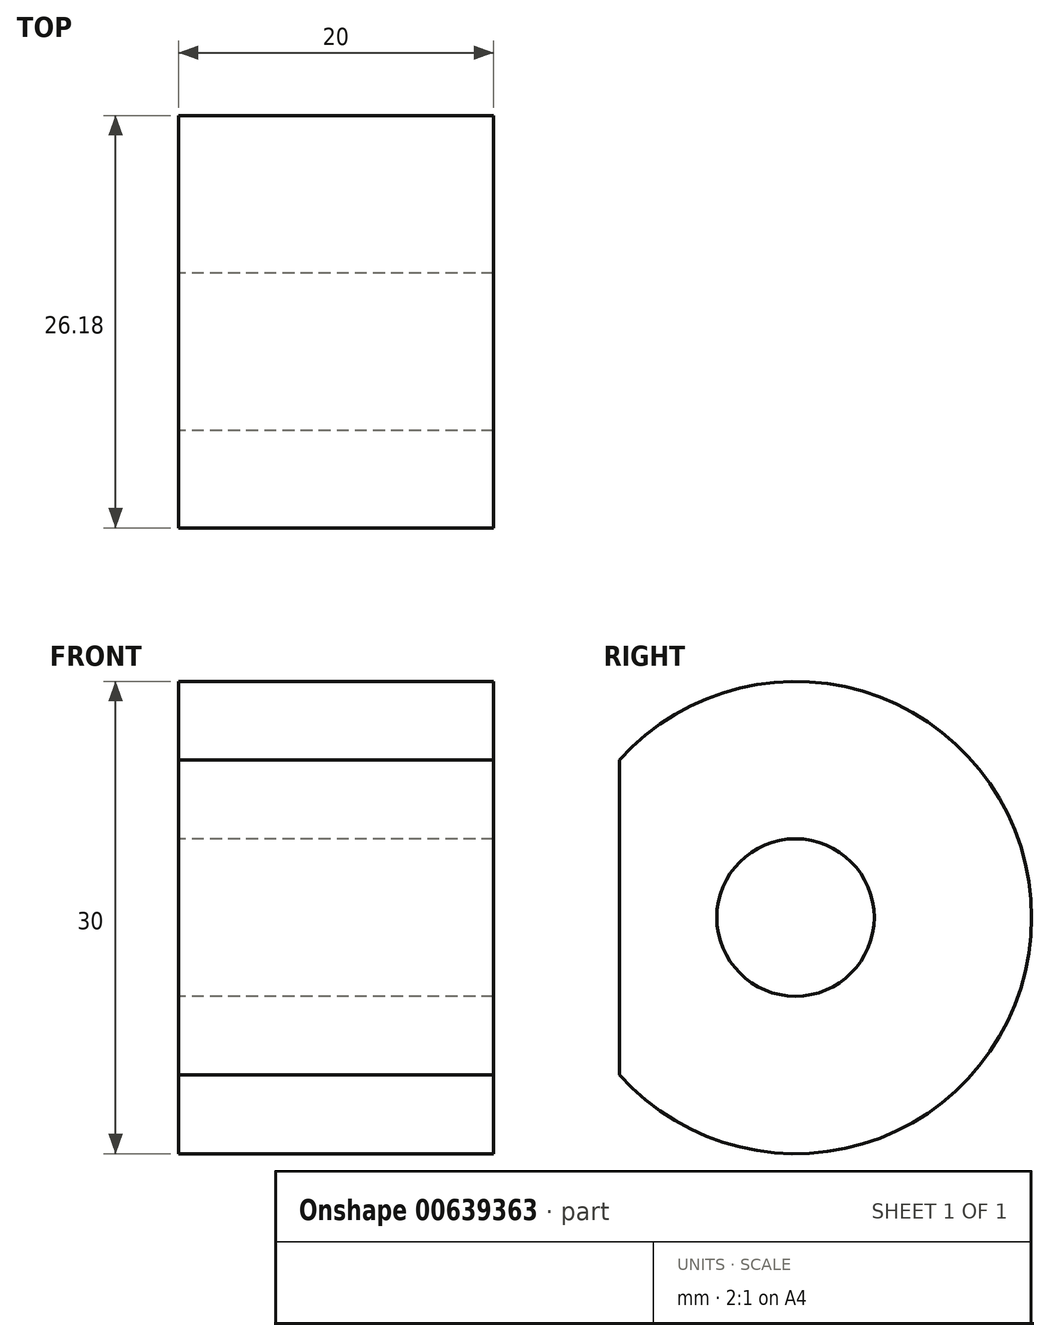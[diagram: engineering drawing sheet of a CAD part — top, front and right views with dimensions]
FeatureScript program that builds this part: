
annotation { "Feature Type Name" : "Feature", "Feature Type Description" : "" }
export const myFeature = defineFeature(function(context is Context, id is Id, definition is map)
    precondition{}
    {
        {
            var Q0;
            Q0=qCreatedBy(makeId("Right.planeOp"),FACE);
            var sketch = newSketch(context, id + "F0", { "sketchPlane" : qUnion([Q0])});
            skCircle(sketch, "E0", {"center": v(0, 0) * mm, "radius": 5 * mm});
            skLineSegment(sketch, "E1", {"start": v(0, 0) * mm, "end": v(0, 5) * mm});
            skLineSegment(sketch, "E2", {"start": v(0, 0) * mm, "end": v(0, -15) * mm});
            skArc(sketch, "E3", {"start": v(-11.18, -10) * mm, "mid": v(15, 0) * mm, "end": v(-11.18, 10) * mm});
            skLineSegment(sketch, "E4", {"start": v(0, 0) * mm, "end": v(-11.18, 0) * mm});
            skLineSegment(sketch, "E5", {"start": v(-11.18, 0) * mm, "end": v(-11.18, 10) * mm});
            skLineSegment(sketch, "E6", {"start": v(-11.18, 10) * mm, "end": v(-11.18, 0) * mm});
            skLineSegment(sketch, "E7", {"start": v(-11.18, 0) * mm, "end": v(-11.18, -10) * mm});
            skLineSegment(sketch, "E8", {"start": v(-11.18, 10) * mm, "end": v(-11.18, -10) * mm});
            skSolve(sketch);
        }
        {
            var Q0;
            Q0=qSketchRegion(id+"F0",true);
            extrude(context, id + "F1", {"entities" : qUnion([Q0]), "depth" : 20 * mm});
        }
    });
